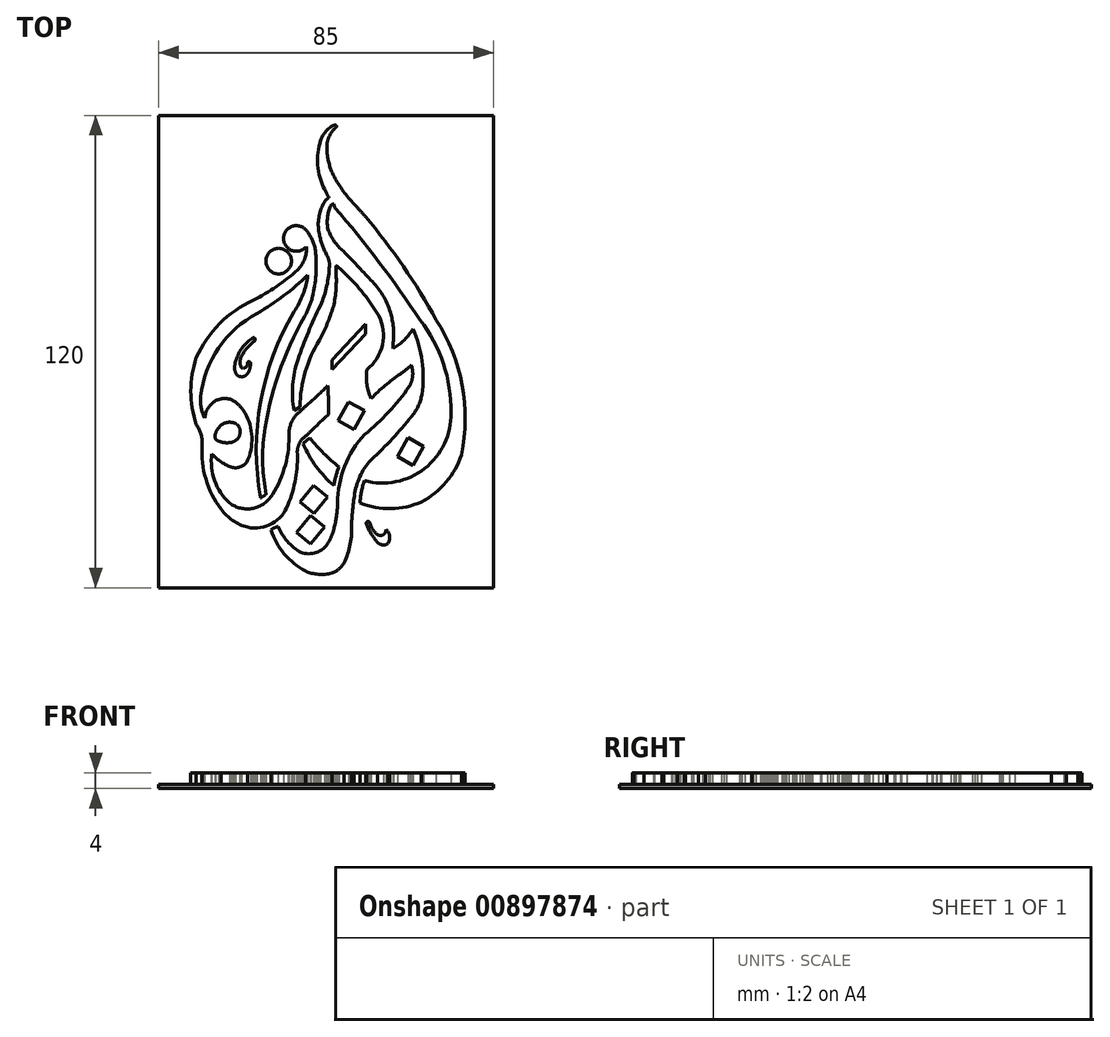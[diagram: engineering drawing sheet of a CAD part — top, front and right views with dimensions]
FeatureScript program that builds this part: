
annotation { "Feature Type Name" : "Feature", "Feature Type Description" : "" }
export const myFeature = defineFeature(function(context is Context, id is Id, definition is map)
    precondition{}
    {
        {
            var Q0;
            Q0=qCreatedBy(makeId("Top.planeOp"),FACE);
            var sketch = newSketch(context, id + "F0", { "sketchPlane" : qUnion([Q0])});
            skArc(sketch, "E0", {"start": v(28, 8) * mm, "mid": v(19.65, 21.6) * mm, "end": v(9.99, 34.31) * mm});
            skArc(sketch, "E1", {"start": v(2.3, 44) * mm, "mid": v(4.71, 40.32) * mm, "end": v(7.57, 36.98) * mm});
            skPoint(sketch, "E2.visualSharp", {"position": v(8.46, 36.1) * mm});
            skArc(sketch, "E2.filletArc", {"start": v(9.99, 34.31) * mm, "mid": v(8.8, 35.67) * mm, "end": v(7.57, 36.98) * mm});
            skArc(sketch, "E3", {"start": v(0.38, 49.73) * mm, "mid": v(1.06, 46.77) * mm, "end": v(2.3, 44) * mm});
            skArc(sketch, "E4", {"start": v(0.38, 53.58) * mm, "mid": v(0.21, 51.65) * mm, "end": v(0.38, 49.73) * mm});
            skArc(sketch, "E5", {"start": v(2.12, 56.56) * mm, "mid": v(1.07, 55.18) * mm, "end": v(0.38, 53.58) * mm});
            skArc(sketch, "E6", {"start": v(-1.56, 52.93) * mm, "mid": v(-2.03, 46.58) * mm, "end": v(0, 40.54) * mm});
            skArc(sketch, "E7", {"start": v(1.53, 57.3) * mm, "mid": v(-0.46, 55.43) * mm, "end": v(-1.56, 52.93) * mm});
            skArc(sketch, "E8", {"start": v(2.74, 57.43) * mm, "mid": v(2.12, 57.5) * mm, "end": v(1.53, 57.3) * mm});
            skArc(sketch, "E9", {"start": v(2.5, 56.88) * mm, "mid": v(2.67, 57.13) * mm, "end": v(2.74, 57.43) * mm});
            skArc(sketch, "E10", {"start": v(2.5, 56.88) * mm, "mid": v(2.3, 56.73) * mm, "end": v(2.12, 56.56) * mm});
            skArc(sketch, "E11", {"start": v(0.78, 39.14) * mm, "mid": v(-0.06, 38.46) * mm, "end": v(-0.66, 37.55) * mm});
            skArc(sketch, "E12", {"start": v(0, 40.54) * mm, "mid": v(0.34, 39.81) * mm, "end": v(0.78, 39.14) * mm});
            skArc(sketch, "E13", {"start": v(-0.84, 37.17) * mm, "mid": v(-1.9, 33.54) * mm, "end": v(-1.7, 29.77) * mm});
            skPoint(sketch, "E14.visualSharp", {"position": v(-0.73, 37.4) * mm});
            skArc(sketch, "E14.filletArc", {"start": v(-0.84, 37.17) * mm, "mid": v(-0.75, 37.36) * mm, "end": v(-0.66, 37.55) * mm});
            skArc(sketch, "E15", {"start": v(-1.7, 29.77) * mm, "mid": v(-0.89, 26.93) * mm, "end": v(0.34, 24.24) * mm});
            skArc(sketch, "E16", {"start": v(0.85, 21.76) * mm, "mid": v(0.76, 23.03) * mm, "end": v(0.34, 24.24) * mm});
            skArc(sketch, "E17", {"start": v(-1.43, 11.7) * mm, "mid": v(0.2, 16.62) * mm, "end": v(0.85, 21.76) * mm});
            skArc(sketch, "E18", {"start": v(-1.43, 11.7) * mm, "mid": v(-4.49, 4.94) * mm, "end": v(-7.14, -1.99) * mm});
            skArc(sketch, "E19", {"start": v(-7.14, -1.99) * mm, "mid": v(-8.47, -8.44) * mm, "end": v(-8.17, -15.02) * mm});
            skLineSegment(sketch, "E20", {"start": v(-8.17, -15.02) * mm, "end": v(-6.65, -14.06) * mm});
            skArc(sketch, "E21", {"start": v(-1.7, 2.92) * mm, "mid": v(-5.3, -5.24) * mm, "end": v(-6.65, -14.06) * mm});
            skArc(sketch, "E22", {"start": v(-1.7, 2.92) * mm, "mid": v(0.32, 7.08) * mm, "end": v(1.86, 11.45) * mm});
            skArc(sketch, "E23", {"start": v(1.86, 11.45) * mm, "mid": v(2.55, 16) * mm, "end": v(2.5, 20.61) * mm});
            skArc(sketch, "E24", {"start": v(10.37, -4.55) * mm, "mid": v(14.32, 1.72) * mm, "end": v(13.42, 9.07) * mm});
            skArc(sketch, "E25", {"start": v(13.2, 9.44) * mm, "mid": v(9, 15.34) * mm, "end": v(4.04, 20.61) * mm});
            skPoint(sketch, "E26.visualSharp", {"position": v(13.3, 9.28) * mm});
            skArc(sketch, "E26.filletArc", {"start": v(13.42, 9.07) * mm, "mid": v(13.32, 9.26) * mm, "end": v(13.2, 9.44) * mm});
            skLineSegment(sketch, "E27", {"start": v(4.04, 20.61) * mm, "end": v(2.81, 21.75) * mm});
            skLineSegment(sketch, "E28", {"start": v(2.5, 21.61) * mm, "end": v(2.5, 20.61) * mm});
            skArc(sketch, "E29", {"start": v(2.81, 21.75) * mm, "mid": v(2.62, 21.77) * mm, "end": v(2.5, 21.61) * mm});
            skPoint(sketch, "E30.orphan", {"position": v(2.5, 22.04) * mm});
            skArc(sketch, "E31", {"start": v(34.37, -26.25) * mm, "mid": v(34.57, -8.5) * mm, "end": v(28, 8) * mm});
            skArc(sketch, "E32", {"start": v(24.3, -38.16) * mm, "mid": v(30.5, -33.19) * mm, "end": v(34.37, -26.25) * mm});
            skArc(sketch, "E33", {"start": v(8.66, -38.49) * mm, "mid": v(16.52, -39.9) * mm, "end": v(24.3, -38.16) * mm});
            skArc(sketch, "E34", {"start": v(9.75, -32.78) * mm, "mid": v(8.98, -35.6) * mm, "end": v(8.66, -38.49) * mm});
            skArc(sketch, "E35", {"start": v(9.75, -32.78) * mm, "mid": v(25.08, -29.7) * mm, "end": v(31.7, -15.55) * mm});
            skArc(sketch, "E36", {"start": v(31.7, -15.55) * mm, "mid": v(29.81, -3.1) * mm, "end": v(23.9, 8) * mm});
            skArc(sketch, "E37", {"start": v(23.9, 8) * mm, "mid": v(13.52, 22.67) * mm, "end": v(2.2, 36.63) * mm});
            skArc(sketch, "E38", {"start": v(2.07, 37.51) * mm, "mid": v(2.09, 37.07) * mm, "end": v(2.2, 36.63) * mm});
            skArc(sketch, "E39", {"start": v(17.05, 2.3) * mm, "mid": v(17.1, 6.15) * mm, "end": v(16.33, 9.93) * mm});
            skArc(sketch, "E40", {"start": v(16.33, 9.93) * mm, "mid": v(14.4, 14.39) * mm, "end": v(11.35, 18.17) * mm});
            skArc(sketch, "E41", {"start": v(11.35, 18.17) * mm, "mid": v(7.92, 21.85) * mm, "end": v(4.46, 25.49) * mm});
            skArc(sketch, "E42", {"start": v(0.52, 31.04) * mm, "mid": v(2.09, 27.98) * mm, "end": v(4.46, 25.49) * mm});
            skArc(sketch, "E43", {"start": v(1.12, 37.02) * mm, "mid": v(0.36, 34.07) * mm, "end": v(0.52, 31.04) * mm});
            skArc(sketch, "E44", {"start": v(2.07, 37.51) * mm, "mid": v(1.53, 37.38) * mm, "end": v(1.12, 37.02) * mm});
            skArc(sketch, "E45", {"start": v(17.05, 2.3) * mm, "mid": v(16.99, 1.53) * mm, "end": v(17.05, 0.76) * mm});
            skArc(sketch, "E46", {"start": v(17.05, 0.76) * mm, "mid": v(19.9, 2.95) * mm, "end": v(22.09, 5.79) * mm});
            skArc(sketch, "E47", {"start": v(24.35, -10.9) * mm, "mid": v(24.41, -2.4) * mm, "end": v(22.09, 5.79) * mm});
            skArc(sketch, "E48", {"start": v(21.6, -16.64) * mm, "mid": v(23.37, -13.95) * mm, "end": v(24.35, -10.9) * mm});
            skArc(sketch, "E49", {"start": v(10.88, -28.02) * mm, "mid": v(16.21, -22.82) * mm, "end": v(21.12, -17.22) * mm});
            skPoint(sketch, "E50.visualSharp", {"position": v(21.4, -16.86) * mm});
            skArc(sketch, "E50.filletArc", {"start": v(21.6, -16.64) * mm, "mid": v(21.36, -16.92) * mm, "end": v(21.12, -17.22) * mm});
            skArc(sketch, "E51", {"start": v(10.88, -28.02) * mm, "mid": v(8.33, -32.38) * mm, "end": v(7.1, -37.29) * mm});
            skArc(sketch, "E52", {"start": v(7.1, -37.29) * mm, "mid": v(6.72, -40.53) * mm, "end": v(6.5, -43.8) * mm});
            skArc(sketch, "E53", {"start": v(4.53, -53.75) * mm, "mid": v(6.16, -48.9) * mm, "end": v(6.5, -43.8) * mm});
            skArc(sketch, "E54", {"start": v(1.49, -56.27) * mm, "mid": v(3.23, -55.28) * mm, "end": v(4.53, -53.75) * mm});
            skArc(sketch, "E55", {"start": v(-5.25, -55.77) * mm, "mid": v(-1.92, -56.59) * mm, "end": v(1.49, -56.27) * mm});
            skArc(sketch, "E56", {"start": v(-13.95, -45.28) * mm, "mid": v(-10.62, -51.37) * mm, "end": v(-5.25, -55.77) * mm});
            skArc(sketch, "E57", {"start": v(-12.14, -44.45) * mm, "mid": v(-13.1, -44.76) * mm, "end": v(-13.95, -45.28) * mm});
            skArc(sketch, "E58", {"start": v(-12.14, -44.45) * mm, "mid": v(-9.83, -48.23) * mm, "end": v(-6.4, -51.02) * mm});
            skArc(sketch, "E59", {"start": v(-6.4, -51.02) * mm, "mid": v(-2.49, -51.04) * mm, "end": v(0.58, -48.6) * mm});
            skArc(sketch, "E60", {"start": v(0.58, -48.6) * mm, "mid": v(1.4, -46.9) * mm, "end": v(2, -45.08) * mm});
            skArc(sketch, "E61", {"start": v(2, -45.08) * mm, "mid": v(2.66, -41.84) * mm, "end": v(2.94, -38.54) * mm});
            skArc(sketch, "E62", {"start": v(9.82, -21.06) * mm, "mid": v(4.72, -29.15) * mm, "end": v(2.94, -38.54) * mm});
            skArc(sketch, "E63", {"start": v(9.82, -21.06) * mm, "mid": v(15.9, -15.38) * mm, "end": v(21.12, -8.9) * mm});
            skArc(sketch, "E64", {"start": v(21.12, -8.9) * mm, "mid": v(21.57, -8.05) * mm, "end": v(21.85, -7.12) * mm});
            skArc(sketch, "E65", {"start": v(10.37, -4.55) * mm, "mid": v(10.38, -8.34) * mm, "end": v(11.49, -11.97) * mm});
            skArc(sketch, "E66", {"start": v(18.93, -5.64) * mm, "mid": v(15.03, -8.59) * mm, "end": v(11.49, -11.97) * mm});
            skArc(sketch, "E67", {"start": v(21.2, -3.87) * mm, "mid": v(21.43, -3.67) * mm, "end": v(21.65, -3.47) * mm});
            skPoint(sketch, "E68.visualSharp", {"position": v(19.94, -4.98) * mm});
            skArc(sketch, "E68.filletArc", {"start": v(18.93, -5.64) * mm, "mid": v(20.1, -4.8) * mm, "end": v(21.2, -3.87) * mm});
            skArc(sketch, "E69", {"start": v(21.85, -7.12) * mm, "mid": v(22.04, -5.28) * mm, "end": v(21.65, -3.47) * mm});
            skArc(sketch, "E70", {"start": v(-5.82, -23.44) * mm, "mid": v(-2.5, -29.2) * mm, "end": v(2, -34.08) * mm});
            skArc(sketch, "E71", {"start": v(-4.08, -21.97) * mm, "mid": v(-5, -22.65) * mm, "end": v(-5.82, -23.44) * mm});
            skArc(sketch, "E72", {"start": v(-4.08, -21.97) * mm, "mid": v(-0.6, -25.85) * mm, "end": v(3.3, -29.3) * mm});
            skArc(sketch, "E73", {"start": v(3.3, -29.3) * mm, "mid": v(2.49, -31.65) * mm, "end": v(2, -34.08) * mm});
            skArc(sketch, "E74", {"start": v(0.62, -16.02) * mm, "mid": v(0.62, -12.32) * mm, "end": v(0.43, -8.62) * mm});
            skArc(sketch, "E75", {"start": v(-4.76, -13.5) * mm, "mid": v(-2.1, -11.14) * mm, "end": v(0.43, -8.62) * mm});
            skArc(sketch, "E76", {"start": v(0.62, -16.02) * mm, "mid": v(-1.63, -18.07) * mm, "end": v(-3.8, -20.2) * mm});
            skArc(sketch, "E77", {"start": v(-7.53, -16.02) * mm, "mid": v(-6.13, -14.77) * mm, "end": v(-4.76, -13.5) * mm});
            skArc(sketch, "E78", {"start": v(-7.53, -16.02) * mm, "mid": v(-8.84, -18.15) * mm, "end": v(-9.42, -20.58) * mm});
            skArc(sketch, "E79", {"start": v(-13.64, -36.3) * mm, "mid": v(-10.31, -28.77) * mm, "end": v(-9.42, -20.58) * mm});
            skArc(sketch, "E80", {"start": v(-24.5, -38.5) * mm, "mid": v(-18.58, -39.82) * mm, "end": v(-13.64, -36.3) * mm});
            skArc(sketch, "E81", {"start": v(-29.02, -25.96) * mm, "mid": v(-28.3, -32.78) * mm, "end": v(-24.5, -38.5) * mm});
            skArc(sketch, "E82", {"start": v(-6.22, -22.4) * mm, "mid": v(-5, -21.31) * mm, "end": v(-3.8, -20.2) * mm});
            skArc(sketch, "E83", {"start": v(-6.22, -22.4) * mm, "mid": v(-6.97, -23.79) * mm, "end": v(-7.31, -25.33) * mm});
            skArc(sketch, "E84", {"start": v(-9.67, -38.9) * mm, "mid": v(-7.72, -32.25) * mm, "end": v(-7.31, -25.33) * mm});
            skArc(sketch, "E85", {"start": v(-19.96, -44.62) * mm, "mid": v(-13.72, -43.73) * mm, "end": v(-9.67, -38.9) * mm});
            skArc(sketch, "E86", {"start": v(-26.65, -40.04) * mm, "mid": v(-23.7, -42.9) * mm, "end": v(-19.96, -44.62) * mm});
            skArc(sketch, "E87", {"start": v(-31.47, -23.92) * mm, "mid": v(-30.54, -32.42) * mm, "end": v(-26.65, -40.04) * mm});
            skArc(sketch, "E88", {"start": v(-31.47, -23.92) * mm, "mid": v(-31.73, -21.09) * mm, "end": v(-32.97, -18.52) * mm});
            skArc(sketch, "E89", {"start": v(-32.97, -1.53) * mm, "mid": v(-34.36, -10.03) * mm, "end": v(-32.97, -18.52) * mm});
            skArc(sketch, "E90", {"start": v(-18.44, 13.06) * mm, "mid": v(-27.04, 7.1) * mm, "end": v(-32.97, -1.53) * mm});
            skArc(sketch, "E91", {"start": v(-18.44, 13.06) * mm, "mid": v(-12.6, 16.54) * mm, "end": v(-7.25, 20.72) * mm});
            skArc(sketch, "E92", {"start": v(-7.25, 20.72) * mm, "mid": v(-5.45, 23.44) * mm, "end": v(-5.02, 26.67) * mm});
            skCircle(sketch, "E93", {"center": v(-12.04, 23) * mm, "radius": 3.25 * mm});
            skArc(sketch, "E94", {"start": v(-4.7, 30.34) * mm, "mid": v(-10.77, 29.02) * mm, "end": v(-5.02, 26.67) * mm});
            skArc(sketch, "E95", {"start": v(-2.65, 24.97) * mm, "mid": v(-3.25, 27.82) * mm, "end": v(-4.7, 30.34) * mm});
            skArc(sketch, "E96", {"start": v(-3.42, 14) * mm, "mid": v(-2.56, 19.45) * mm, "end": v(-2.65, 24.97) * mm});
            skArc(sketch, "E97", {"start": v(-5.45, 8.9) * mm, "mid": v(-12.06, -5.75) * mm, "end": v(-15.8, -21.37) * mm});
            skPoint(sketch, "E98.visualSharp", {"position": v(-4.46, 10.6) * mm});
            skArc(sketch, "E98.filletArc", {"start": v(-5.45, 8.9) * mm, "mid": v(-4.26, 11.38) * mm, "end": v(-3.42, 14) * mm});
            skArc(sketch, "E99", {"start": v(-15.8, -21.37) * mm, "mid": v(-16.08, -28.86) * mm, "end": v(-15.22, -36.3) * mm});
            skArc(sketch, "E100", {"start": v(-15.22, -36.3) * mm, "mid": v(-15.93, -36.74) * mm, "end": v(-16.62, -37.2) * mm});
            skArc(sketch, "E101", {"start": v(-8.1, 10.13) * mm, "mid": v(-16.64, -12.77) * mm, "end": v(-16.62, -37.2) * mm});
            skArc(sketch, "E102", {"start": v(-8.1, 10.13) * mm, "mid": v(-5.82, 14.58) * mm, "end": v(-4.66, 19.46) * mm});
            skArc(sketch, "E103", {"start": v(-17.5, 9.71) * mm, "mid": v(-10.78, 14.2) * mm, "end": v(-4.66, 19.46) * mm});
            skArc(sketch, "E104", {"start": v(-17.5, 9.71) * mm, "mid": v(-27.26, 0.9) * mm, "end": v(-31.88, -11.4) * mm});
            skArc(sketch, "E105", {"start": v(-31.88, -11.4) * mm, "mid": v(-31.73, -14.22) * mm, "end": v(-30.83, -16.88) * mm});
            skArc(sketch, "E106", {"start": v(-28.04, -12.47) * mm, "mid": v(-29.96, -14.34) * mm, "end": v(-30.83, -16.88) * mm});
            skArc(sketch, "E107", {"start": v(-24.15, -12.17) * mm, "mid": v(-26.12, -11.95) * mm, "end": v(-28.04, -12.47) * mm});
            skArc(sketch, "E108", {"start": v(-21.06, -14.89) * mm, "mid": v(-22.42, -13.32) * mm, "end": v(-24.15, -12.17) * mm});
            skArc(sketch, "E109", {"start": v(-19.75, -27.3) * mm, "mid": v(-18.9, -20.94) * mm, "end": v(-21.06, -14.89) * mm});
            skArc(sketch, "E110", {"start": v(-23.77, -29.44) * mm, "mid": v(-21.36, -29.12) * mm, "end": v(-19.75, -27.3) * mm});
            skArc(sketch, "E111", {"start": v(-29.02, -25.96) * mm, "mid": v(-26.64, -28.07) * mm, "end": v(-23.77, -29.44) * mm});
            skArc(sketch, "E112", {"start": v(-22.97, -18.28) * mm, "mid": v(-24.84, -17.96) * mm, "end": v(-26.6, -18.65) * mm});
            skArc(sketch, "E113", {"start": v(-21.98, -21.4) * mm, "mid": v(-21.84, -20.56) * mm, "end": v(-21.9, -19.71) * mm});
            skArc(sketch, "E114", {"start": v(-23.8, -23.03) * mm, "mid": v(-22.73, -22.4) * mm, "end": v(-21.98, -21.4) * mm});
            skArc(sketch, "E115", {"start": v(-27.35, -22.76) * mm, "mid": v(-25.6, -23.15) * mm, "end": v(-23.8, -23.03) * mm});
            skArc(sketch, "E116", {"start": v(-26.6, -18.65) * mm, "mid": v(-27.52, -19.63) * mm, "end": v(-28.1, -20.85) * mm});
            skArc(sketch, "E117", {"start": v(-27.89, -22.42) * mm, "mid": v(-27.64, -22.61) * mm, "end": v(-27.35, -22.76) * mm});
            skArc(sketch, "E118", {"start": v(-28.1, -20.85) * mm, "mid": v(-28.2, -21.32) * mm, "end": v(-28.19, -21.8) * mm});
            skArc(sketch, "E119", {"start": v(-21.9, -19.71) * mm, "mid": v(-22.28, -18.88) * mm, "end": v(-22.97, -18.28) * mm});
            skPoint(sketch, "E120.visualSharp", {"position": v(-28.13, -22.1) * mm});
            skArc(sketch, "E120.filletArc", {"start": v(-28.19, -21.8) * mm, "mid": v(-28.1, -22.14) * mm, "end": v(-27.89, -22.42) * mm});
            skLineSegment(sketch, "E121", {"start": v(1.5, -2.1) * mm, "end": v(1.5, -4.61) * mm});
            skLineSegment(sketch, "E122", {"start": v(1.5, -4.61) * mm, "end": v(9.98, 4.45) * mm});
            skLineSegment(sketch, "E123", {"start": v(9.98, 4.45) * mm, "end": v(9.98, 6.97) * mm});
            skLineSegment(sketch, "E124", {"start": v(9.98, 6.97) * mm, "end": v(1.5, -2.1) * mm});
            skLineSegment(sketch, "E125", {"start": v(3.08, -17.5) * mm, "end": v(5.75, -12.75) * mm});
            skLineSegment(sketch, "E126", {"start": v(5.75, -12.75) * mm, "end": v(9.77, -15) * mm});
            skLineSegment(sketch, "E127", {"start": v(9.77, -15) * mm, "end": v(7.1, -19.76) * mm});
            skLineSegment(sketch, "E128", {"start": v(7.1, -19.76) * mm, "end": v(3.08, -17.5) * mm});
            skLineSegment(sketch, "E129", {"start": v(18.1, -26.63) * mm, "end": v(20.78, -21.88) * mm});
            skLineSegment(sketch, "E130", {"start": v(20.78, -21.88) * mm, "end": v(24.8, -24.14) * mm});
            skLineSegment(sketch, "E131", {"start": v(24.8, -24.14) * mm, "end": v(22.12, -28.89) * mm});
            skLineSegment(sketch, "E132", {"start": v(22.12, -28.89) * mm, "end": v(18.1, -26.63) * mm});
            skLineSegment(sketch, "E133", {"start": v(-6.65, -38.25) * mm, "end": v(-3.19, -34.04) * mm});
            skLineSegment(sketch, "E134", {"start": v(-3.19, -34.04) * mm, "end": v(0.37, -36.96) * mm});
            skLineSegment(sketch, "E135", {"start": v(0.37, -36.96) * mm, "end": v(-3.09, -41.18) * mm});
            skLineSegment(sketch, "E136", {"start": v(-3.09, -41.18) * mm, "end": v(-6.65, -38.25) * mm});
            skLineSegment(sketch, "E137", {"start": v(-7.43, -45.9) * mm, "end": v(-3.98, -41.69) * mm});
            skLineSegment(sketch, "E138", {"start": v(-3.98, -41.69) * mm, "end": v(-0.42, -44.6) * mm});
            skLineSegment(sketch, "E139", {"start": v(-0.42, -44.6) * mm, "end": v(-3.87, -48.82) * mm});
            skLineSegment(sketch, "E140", {"start": v(-3.87, -48.82) * mm, "end": v(-7.43, -45.9) * mm});
            skArc(sketch, "E141", {"start": v(-18.74, 3.38) * mm, "mid": v(-21.66, 0.41) * mm, "end": v(-23.17, -3.46) * mm});
            skArc(sketch, "E142", {"start": v(-23.17, -3.46) * mm, "mid": v(-23.2, -4.56) * mm, "end": v(-22.88, -5.61) * mm});
            skArc(sketch, "E143", {"start": v(-22.7, -5.87) * mm, "mid": v(-21.34, -6.4) * mm, "end": v(-20.05, -5.74) * mm});
            skPoint(sketch, "E144.visualSharp", {"position": v(-22.81, -5.74) * mm});
            skArc(sketch, "E144.filletArc", {"start": v(-22.88, -5.61) * mm, "mid": v(-22.8, -5.75) * mm, "end": v(-22.7, -5.87) * mm});
            skArc(sketch, "E145", {"start": v(-20.05, -5.74) * mm, "mid": v(-19.4, -4.48) * mm, "end": v(-19.21, -3.08) * mm});
            skArc(sketch, "E146", {"start": v(-18.12, 2.72) * mm, "mid": v(-18.09, 3.38) * mm, "end": v(-18.74, 3.38) * mm});
            skArc(sketch, "E147", {"start": v(-18.12, 2.72) * mm, "mid": v(-19.98, 0.97) * mm, "end": v(-21.46, -1.11) * mm});
            skArc(sketch, "E148", {"start": v(-21.46, -1.11) * mm, "mid": v(-21.84, -2.51) * mm, "end": v(-21.58, -3.94) * mm});
            skArc(sketch, "E149", {"start": v(-21.11, -4.25) * mm, "mid": v(-20.32, -3.92) * mm, "end": v(-19.96, -3.15) * mm});
            skPoint(sketch, "E150.visualSharp", {"position": v(-21.46, -4.2) * mm});
            skArc(sketch, "E150.filletArc", {"start": v(-21.58, -3.94) * mm, "mid": v(-21.4, -4.16) * mm, "end": v(-21.11, -4.25) * mm});
            skArc(sketch, "E151", {"start": v(-19.21, -3.08) * mm, "mid": v(-19.63, -2.58) * mm, "end": v(-19.96, -3.15) * mm});
            skArc(sketch, "E152", {"start": v(10.3, -43.86) * mm, "mid": v(11.5, -46.3) * mm, "end": v(13.12, -48.47) * mm});
            skArc(sketch, "E153", {"start": v(13.12, -48.47) * mm, "mid": v(14.36, -49.12) * mm, "end": v(15.71, -48.76) * mm});
            skArc(sketch, "E154", {"start": v(15.71, -48.76) * mm, "mid": v(16.13, -46.87) * mm, "end": v(15.2, -45.16) * mm});
            skArc(sketch, "E155", {"start": v(12.97, -46.46) * mm, "mid": v(14.5, -46.54) * mm, "end": v(15.2, -45.16) * mm});
            skArc(sketch, "E156", {"start": v(11.11, -43.46) * mm, "mid": v(11.84, -45.09) * mm, "end": v(12.97, -46.46) * mm});
            skArc(sketch, "E157", {"start": v(11.11, -43.46) * mm, "mid": v(10.48, -43.2) * mm, "end": v(10.3, -43.86) * mm});
            skSolve(sketch);
        }
        {
            var Q0;
            Q0 = qSketchRegion(id + "F0", true);
            extrude(context, id + "F1", {"entities" : qUnion([Q0]), "depth" : 3 * mm, "offsetDistance" : 25 * mm});
        }
        {
            var Q0;
            Q0=qCreatedBy(makeId("Top.planeOp"),FACE);
            var sketch = newSketch(context, id + "F2", { "sketchPlane" : qUnion([Q0])});
            skLineSegment(sketch, "E158.bottom", {"start": v(42.5, 60) * mm, "end": v(-42.5, 60) * mm});
            skLineSegment(sketch, "E158.top", {"start": v(42.5, -60) * mm, "end": v(-42.5, -60) * mm});
            skLineSegment(sketch, "E158.left", {"start": v(42.5, 60) * mm, "end": v(42.5, -60) * mm});
            skLineSegment(sketch, "E158.right", {"start": v(-42.5, 60) * mm, "end": v(-42.5, -60) * mm});
            skPoint(sketch, "E158.middle", {"position": v(0, 0) * mm});
            skSolve(sketch);
        }
        {
            var Q0;
            Q0 = qSketchRegion(id + "F2", true);
            extrude(context, id + "F3", {"entities" : qUnion([Q0]), "operationType" : NewBodyOperationType.ADD, "oppositeDirection" : true, "depth" : 1 * mm, "offsetDistance" : 25 * mm});
        }
    });
